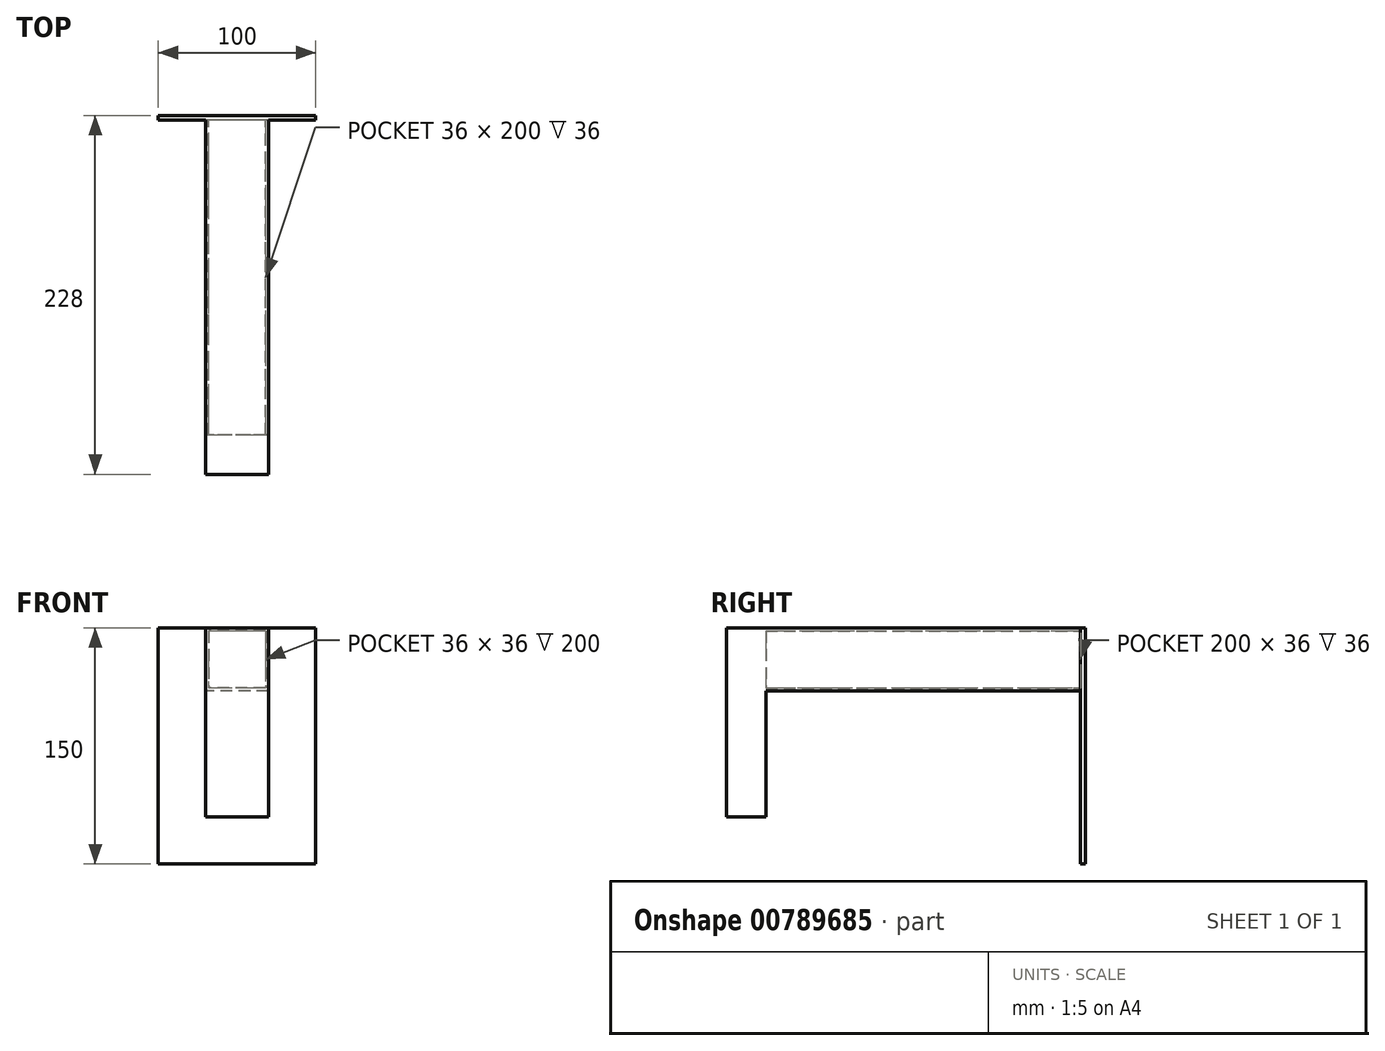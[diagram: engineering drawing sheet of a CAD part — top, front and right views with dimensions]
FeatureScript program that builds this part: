
annotation { "Feature Type Name" : "Feature", "Feature Type Description" : "" }
export const myFeature = defineFeature(function(context is Context, id is Id, definition is map)
    precondition{}
    {
        {
            var Q0;
            Q0=qCreatedBy(makeId("Front.planeOp"),FACE);
            var sketch = newSketch(context, id + "F0", { "sketchPlane" : qUnion([Q0])});
            skLineSegment(sketch, "E0.bottom", {"start": v(50, 75) * mm, "end": v(-50, 75) * mm});
            skLineSegment(sketch, "E0.top", {"start": v(50, -75) * mm, "end": v(-50, -75) * mm});
            skLineSegment(sketch, "E0.left", {"start": v(50, 75) * mm, "end": v(50, -75) * mm});
            skLineSegment(sketch, "E0.right", {"start": v(-50, 75) * mm, "end": v(-50, -75) * mm});
            skPoint(sketch, "E0.middle", {"position": v(0, 0) * mm});
            skSolve(sketch);
        }
        {
            var Q0;
            Q0 = qSketchRegion(id + "F0", true);
            extrude(context, id + "F1", {"entities" : qUnion([Q0]), "depth" : 3 * mm, "offsetDistance" : 25 * mm});
        }
        {
            var Q0;
            Q0=makeQuery(id+"F1.opExtrude","CAP_FACE",FACE,{"disambiguationData":[OSD([sQuery(id+"F0.wireOp",EDGE,"E0.bottom"),sQuery(id+"F0.wireOp",EDGE,"E0.top"),sQuery(id+"F0.wireOp",EDGE,"E0.left"),sQuery(id+"F0.wireOp",EDGE,"E0.right")])],"isStart":false});
            var sketch = newSketch(context, id + "F2", { "sketchPlane" : qUnion([Q0])});
            skPoint(sketch, "E1", {"position": v(0, 75) * mm});
            skLineSegment(sketch, "E2", {"start": v(0, 75) * mm, "end": v(20, 75) * mm});
            skLineSegment(sketch, "E3", {"start": v(20, 75) * mm, "end": v(20, 35) * mm});
            skLineSegment(sketch, "E4", {"start": v(20, 35) * mm, "end": v(-20, 35) * mm});
            skLineSegment(sketch, "E5", {"start": v(-20, 35) * mm, "end": v(-20, 75) * mm});
            skLineSegment(sketch, "E6", {"start": v(-20, 75) * mm, "end": v(0, 75) * mm});
            skPoint(sketch, "E7", {"position": v(0, 55) * mm});
            skPoint(sketch, "E7.positionSnap0", {"position": v(-20, 55) * mm});
            skLineSegment(sketch, "E8.bottom", {"start": v(18, 73) * mm, "end": v(-18, 73) * mm});
            skLineSegment(sketch, "E8.top", {"start": v(18, 37) * mm, "end": v(-18, 37) * mm});
            skLineSegment(sketch, "E8.left", {"start": v(18, 73) * mm, "end": v(18, 37) * mm});
            skLineSegment(sketch, "E8.right", {"start": v(-18, 73) * mm, "end": v(-18, 37) * mm});
            skSolve(sketch);
        }
        {
            var Q0;
            Q0 = qSketchRegion(id + "F2", true);
            extrude(context, id + "F3", {"entities" : qUnion([Q0]), "operationType" : NewBodyOperationType.ADD, "depth" : 200 * mm, "offsetDistance" : 25 * mm});
        }
        {
            var Q0;
            Q0=makeQuery(id+"F3.opExtrude","CAP_FACE",FACE,{"disambiguationData":[OSD([sQuery(id+"F2.wireOp",EDGE,"E2"),sQuery(id+"F2.wireOp",EDGE,"E3"),sQuery(id+"F2.wireOp",EDGE,"E4"),sQuery(id+"F2.wireOp",EDGE,"E5"),sQuery(id+"F2.wireOp",EDGE,"E6"),sQuery(id+"F2.wireOp",EDGE,"E8.bottom"),sQuery(id+"F2.wireOp",EDGE,"E8.top"),sQuery(id+"F2.wireOp",EDGE,"E8.left"),sQuery(id+"F2.wireOp",EDGE,"E8.right")])],"isStart":false});
            var sketch = newSketch(context, id + "F4", { "sketchPlane" : qUnion([Q0])});
            skPoint(sketch, "E9", {"position": v(-20, 75) * mm});
            skLineSegment(sketch, "E10", {"start": v(-20, 75) * mm, "end": v(-20, -45) * mm});
            skLineSegment(sketch, "E11", {"start": v(-20, -45) * mm, "end": v(20, -45) * mm});
            skLineSegment(sketch, "E12", {"start": v(20, -45) * mm, "end": v(20, 75) * mm});
            skLineSegment(sketch, "E13", {"start": v(20, 75) * mm, "end": v(-20, 75) * mm});
            skSolve(sketch);
        }
        {
            var Q0;
            Q0 = qSketchRegion(id + "F4", true);
            extrude(context, id + "F5", {"entities" : qUnion([Q0]), "operationType" : NewBodyOperationType.ADD, "depth" : 25 * mm, "offsetDistance" : 25 * mm});
        }
    });
